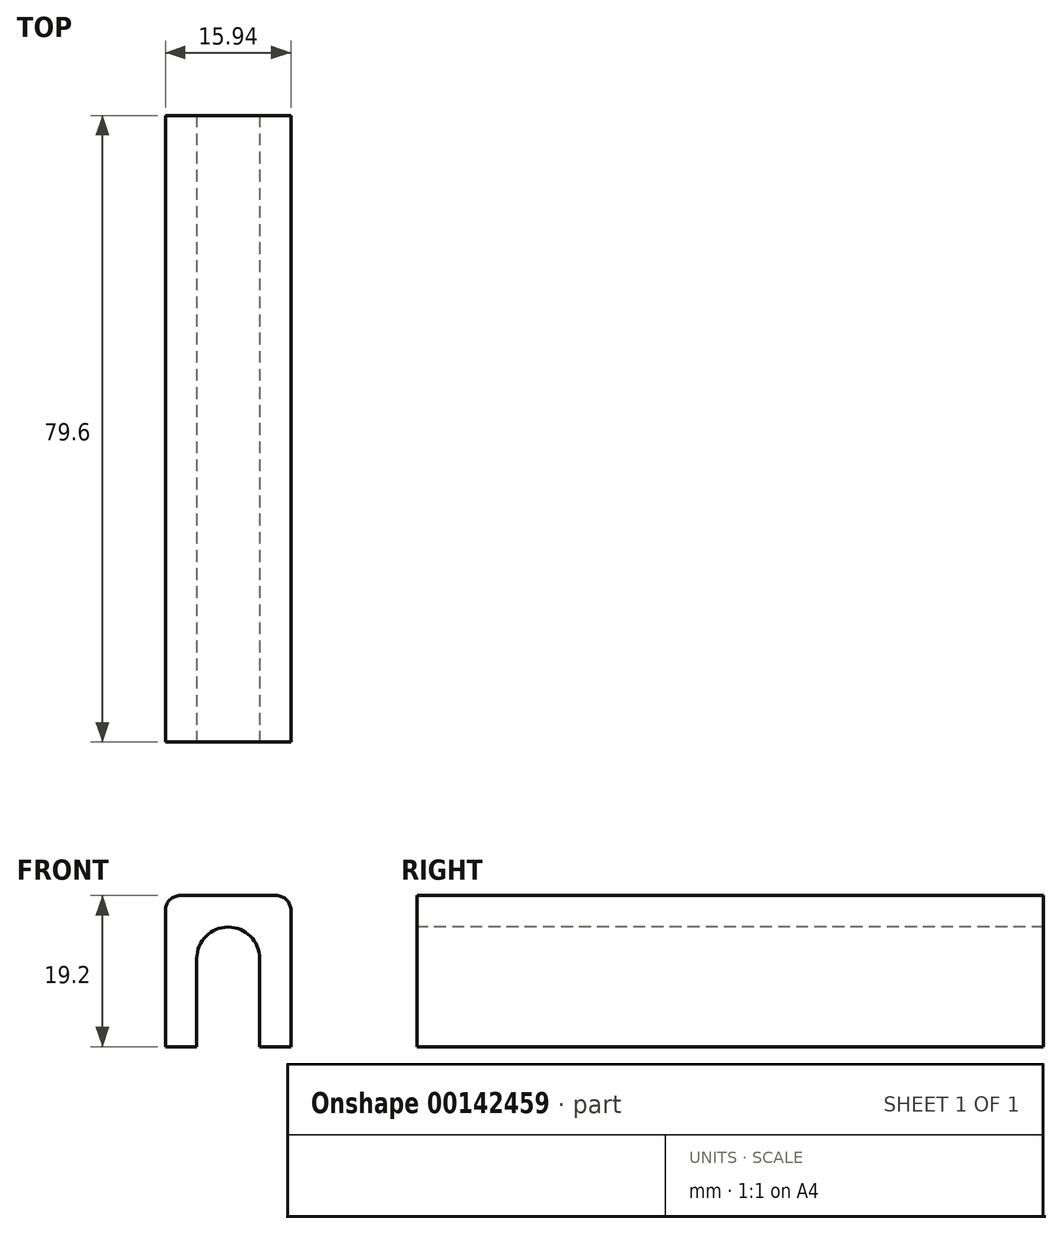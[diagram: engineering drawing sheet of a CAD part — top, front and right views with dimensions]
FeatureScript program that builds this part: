
annotation { "Feature Type Name" : "Feature", "Feature Type Description" : "" }
export const myFeature = defineFeature(function(context is Context, id is Id, definition is map)
    precondition{}
    {
        {
            var Q0;
            Q0=qCreatedBy(makeId("Front.planeOp"),FACE);
            var sketch = newSketch(context, id + "F0", { "sketchPlane" : qUnion([Q0])});
            skLineSegment(sketch, "E0.bottom", {"start": v(-7.97, -11.2) * mm, "end": v(7.97, -11.2) * mm});
            skLineSegment(sketch, "E0.top", {"start": v(-7.97, 8) * mm, "end": v(7.97, 8) * mm});
            skLineSegment(sketch, "E0.left", {"start": v(-7.97, -11.2) * mm, "end": v(-7.97, 8) * mm});
            skLineSegment(sketch, "E0.right", {"start": v(7.97, -11.2) * mm, "end": v(7.97, 8) * mm});
            skSolve(sketch);
        }
        {
            var Q0;
            Q0 = qSketchRegion(id + "F0", true);
            extrude(context, id + "F1", {"entities" : qUnion([Q0]), "oppositeDirection" : true, "depth" : 79.6 * mm});
        }
        {
            var Q0;
            Q0=makeQuery(id+"F1.opExtrude","SWEPT_EDGE",EDGE,{"disambiguationData":[OSD([sQuery(id+"F0.wireOp",EDGE,"E0.top"),sQuery(id+"F0.wireOp",EDGE,"E0.right")])]});
            var Q1;
            Q1=makeQuery(id+"F1.opExtrude","SWEPT_EDGE",EDGE,{"disambiguationData":[OSD([sQuery(id+"F0.wireOp",EDGE,"E0.top"),sQuery(id+"F0.wireOp",EDGE,"E0.left")])]});
            fillet(context, id + "F2", {"entities" : qUnion([Q0, Q1]), "radius" : 1.9 * mm, "tangentPropagation" : true, "allowEdgeOverflow" : false});
        }
        {
            var Q0;
            Q0=makeQuery(id+"F1.opExtrude","CAP_FACE",FACE,{"disambiguationData":[OSD([sQuery(id+"F0.wireOp",EDGE,"E0.bottom"),sQuery(id+"F0.wireOp",EDGE,"E0.top"),sQuery(id+"F0.wireOp",EDGE,"E0.left"),sQuery(id+"F0.wireOp",EDGE,"E0.right")])],"isStart":true});
            var sketch = newSketch(context, id + "F3", { "sketchPlane" : qUnion([Q0])});
            skLineSegment(sketch, "E1.bottom", {"start": v(-4, -11.2) * mm, "end": v(4, -11.2) * mm});
            skLineSegment(sketch, "E1.top", {"start": v(-4, 4) * mm, "end": v(4, 4) * mm});
            skLineSegment(sketch, "E1.left", {"start": v(-4, -11.2) * mm, "end": v(-4, 4) * mm});
            skLineSegment(sketch, "E1.right", {"start": v(4, -11.2) * mm, "end": v(4, 4) * mm});
            skSolve(sketch);
        }
        {
            var Q0;
            Q0 = qSketchRegion(id + "F3", true);
            extrude(context, id + "F4", {"entities" : qUnion([Q0]), "operationType" : NewBodyOperationType.REMOVE, "endBound" : BoundingType.THROUGH_ALL, "oppositeDirection" : true, "depth" : 25 * mm});
        }
        {
            var Q0;
            Q0=makeQuery(id+"F4.boolean.opBoolean","COPY",EDGE,{"derivedFrom":makeQuery(id+"F4.opExtrude","SWEPT_EDGE",EDGE,{"disambiguationData":[OSD([sQuery(id+"F3.wireOp",EDGE,"E1.top"),sQuery(id+"F3.wireOp",EDGE,"E1.right")])]})});
            var Q1;
            Q1=makeQuery(id+"F4.boolean.opBoolean","COPY",EDGE,{"derivedFrom":makeQuery(id+"F4.opExtrude","SWEPT_EDGE",EDGE,{"disambiguationData":[OSD([sQuery(id+"F3.wireOp",EDGE,"E1.top"),sQuery(id+"F3.wireOp",EDGE,"E1.left")])]})});
            fillet(context, id + "F5", {"entities" : qUnion([Q0, Q1]), "radius" : 4 * mm, "tangentPropagation" : true, "allowEdgeOverflow" : false});
        }
    });
